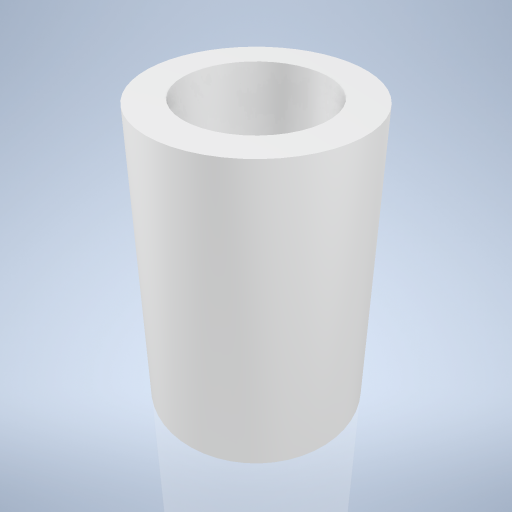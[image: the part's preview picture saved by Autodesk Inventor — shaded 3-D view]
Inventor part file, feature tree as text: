
AUTODESK INVENTOR PART (.ipt)
format: ipt  version: 2024.2 (Build 282272000, 272)  size: 231,424 bytes
history: native  units: mm
features: extrude x2, sketch x2
ambient origin geometry x8: Origin, YZ Plane, XZ Plane, XY Plane, X Axis, Y Axis, Z Axis, Center Point
bodies: Volumenkörper1 (feature_tree)
feature tree (4):
  extrude  "Extrusion1"  Depth=11.0mm TaperAngle=0.0deg
  extrude  "Extrusion2"  Depth=11.0mm TaperAngle=0.0deg
  sketch  "Skizze1"  dims[d0=7.5mm d1=11.0mm d2=0.0mm]
  sketch  "Skizze2"  dims[d3=5.0mm d4=11.0mm d5=0.0mm]
